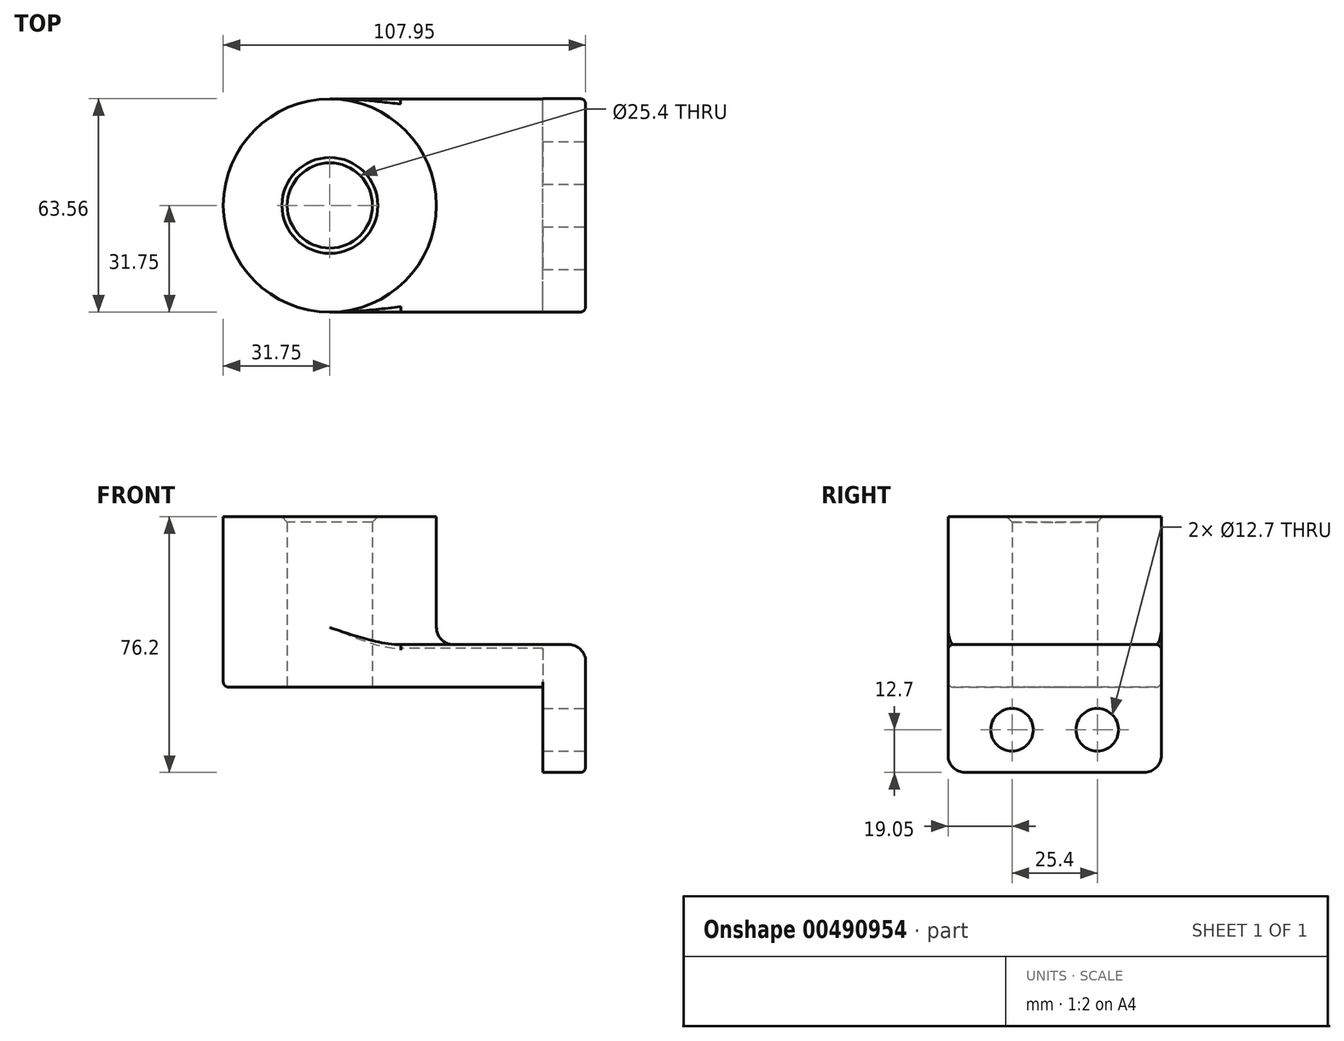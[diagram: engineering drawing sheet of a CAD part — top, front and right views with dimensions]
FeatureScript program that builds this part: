
annotation { "Feature Type Name" : "Feature", "Feature Type Description" : "" }
export const myFeature = defineFeature(function(context is Context, id is Id, definition is map)
    precondition{}
    {
        {
            var Q0;
            Q0=qCreatedBy(makeId("Top.planeOp"),FACE);
            var sketch = newSketch(context, id + "F0", { "sketchPlane" : qUnion([Q0])});
            skLineSegment(sketch, "E0.bottom", {"start": v(-38.1, 31.75) * mm, "end": v(38.1, 31.75) * mm});
            skLineSegment(sketch, "E0.top", {"start": v(-38.1, -31.75) * mm, "end": v(38.1, -31.75) * mm});
            skLineSegment(sketch, "E0.left", {"start": v(-38.1, 31.75) * mm, "end": v(-38.1, -31.75) * mm});
            skLineSegment(sketch, "E0.right", {"start": v(38.1, 31.75) * mm, "end": v(38.1, -31.75) * mm});
            skPoint(sketch, "E0.middle", {"position": v(0, 0) * mm});
            skCircle(sketch, "E1", {"center": v(-38.1, 0) * mm, "radius": 31.75 * mm});
            skCircle(sketch, "E2", {"center": v(-38.1, 0) * mm, "radius": 12.7 * mm});
            skSolve(sketch);
        }
        {
            var Q0;
            {var subQ0=sQuery(id+"F0.wireOp",EDGE,"E0.bottom");Q0=makeQuery(id+"F0.imprint","IMPRINT",FACE,{"disambiguationData":[TD([[makeQuery(id+"F0.imprint","IMPRINT",EDGE,{"derivedFrom":subQ0}),-1.0]])]});}
            var Q1;
            {var subQ1=sQuery(id+"F0.wireOp",EDGE,"E0.left");var subQ3=sQuery(id+"F0.wireOp",EDGE,"E2");var subQ4=makeQuery(id+"F0.imprint","INTERSECT",VERTEX,{"disambiguationData":[OD(0.0)],"derivedFrom":[subQ1,subQ3]});Q1=makeQuery(id+"F0.imprint","IMPRINT",FACE,{"disambiguationData":[TD([[makeQuery(id+"F0.imprint","IMPRINT",EDGE,{"disambiguationData":[TD([[subQ4,1.0]])],"derivedFrom":subQ3}),-1.0]])]});}
            var Q2;
            {var subQ1=sQuery(id+"F0.wireOp",EDGE,"E0.left");var subQ3=sQuery(id+"F0.wireOp",EDGE,"E2");var subQ4=makeQuery(id+"F0.imprint","INTERSECT",VERTEX,{"disambiguationData":[OD(0.0)],"derivedFrom":[subQ1,subQ3]});Q2=makeQuery(id+"F0.imprint","IMPRINT",FACE,{"disambiguationData":[TD([[makeQuery(id+"F0.imprint","IMPRINT",EDGE,{"disambiguationData":[TD([[subQ4,-1.0]])],"derivedFrom":subQ3}),-1.0]])]});}
            extrude(context, id + "F1", {"entities" : qUnion([Q0, Q1, Q2]), "depth" : 12.7 * mm});
        }
        {
            var Q0;
            {var subQ1=sQuery(id+"F0.wireOp",EDGE,"E0.left");var subQ3=sQuery(id+"F0.wireOp",EDGE,"E2");var subQ4=makeQuery(id+"F0.imprint","INTERSECT",VERTEX,{"disambiguationData":[OD(0.0)],"derivedFrom":[subQ1,subQ3]});Q0=makeQuery(id+"F0.imprint","IMPRINT",FACE,{"disambiguationData":[TD([[makeQuery(id+"F0.imprint","IMPRINT",EDGE,{"disambiguationData":[TD([[subQ4,-1.0]])],"derivedFrom":subQ3}),-1.0]])]});}
            var Q1;
            {var subQ1=sQuery(id+"F0.wireOp",EDGE,"E0.left");var subQ3=sQuery(id+"F0.wireOp",EDGE,"E2");var subQ4=makeQuery(id+"F0.imprint","INTERSECT",VERTEX,{"disambiguationData":[OD(0.0)],"derivedFrom":[subQ1,subQ3]});Q1=makeQuery(id+"F0.imprint","IMPRINT",FACE,{"disambiguationData":[TD([[makeQuery(id+"F0.imprint","IMPRINT",EDGE,{"disambiguationData":[TD([[subQ4,1.0]])],"derivedFrom":subQ3}),-1.0]])]});}
            extrude(context, id + "F2", {"entities" : qUnion([Q0, Q1]), "operationType" : NewBodyOperationType.ADD, "depth" : 50.8 * mm});
        }
        {
            var Q0;
            Q0=makeQuery(id+"F1.opExtrude","SWEPT_FACE",FACE,{"disambiguationData":[OSD([sQuery(id+"F0.wireOp",EDGE,"E0.right")])]});
            var sketch = newSketch(context, id + "F3", { "sketchPlane" : qUnion([Q0])});
            skLineSegment(sketch, "E3.bottom", {"start": v(-31.75, 12.7) * mm, "end": v(31.81, 12.7) * mm});
            skLineSegment(sketch, "E3.top", {"start": v(-31.75, -25.4) * mm, "end": v(31.81, -25.4) * mm});
            skLineSegment(sketch, "E3.left", {"start": v(-31.75, 12.7) * mm, "end": v(-31.75, -25.4) * mm});
            skLineSegment(sketch, "E3.right", {"start": v(31.81, 12.7) * mm, "end": v(31.81, -25.4) * mm});
            skCircle(sketch, "E4", {"center": v(-12.7, -12.7) * mm, "radius": 6.35 * mm});
            skLineSegment(sketch, "E5", {"start": v(0, 12.7) * mm, "end": v(0, -25.4) * mm});
            skCircle(sketch, "E6.MirrorC", {"center": v(12.7, -12.7) * mm, "radius": 6.35 * mm});
            skSolve(sketch);
        }
        {
            var Q0;
            {var subQ0=sQuery(id+"F3.wireOp",EDGE,"E3.left");var subQ1=sQuery(id+"F3.wireOp",EDGE,"E3.bottom");var subQ2=makeQuery(id+"F3.imprint","INTERSECT",VERTEX,{"derivedFrom":[subQ1,subQ0]});Q0=makeQuery(id+"F3.imprint","IMPRINT",FACE,{"disambiguationData":[TD([[makeQuery(id+"F3.imprint","IMPRINT",EDGE,{"disambiguationData":[TD([[subQ2,1.0]])],"derivedFrom":subQ1}),1.0]])]});}
            var Q1;
            {var subQ1=sQuery(id+"F0.wireOp",EDGE,"E0.right");var subQ2=makeQuery(id+"F1.opExtrude","SWEPT_EDGE",EDGE,{"disambiguationData":[OSD([sQuery(id+"F0.wireOp",EDGE,"E0.bottom"),subQ1])]});Q1=makeQuery(id+"F3.imprint","IMPRINT",FACE,{"disambiguationData":[TD([[makeQuery(id+"F3.imprint","IMPRINT",EDGE,{"derivedFrom":subQ2}),-1.0]])]});}
            var Q2;
            {var subQ6=sQuery(id+"F3.wireOp",EDGE,"E3.right");Q2=makeQuery(id+"F3.imprint","IMPRINT",FACE,{"disambiguationData":[TD([[makeQuery(id+"F3.imprint","IMPRINT",EDGE,{"derivedFrom":subQ6}),-1.0]])]});}
            var Q3;
            Q3=makeQuery(id+"F3.imprint","IMPRINT",FACE,{"disambiguationData":[TD([[makeQuery(id+"F3.imprint","IMPRINT",EDGE,{"derivedFrom":sQuery(id+"F3.wireOp",EDGE,"E4")}),-1.0]])]});
            extrude(context, id + "F4", {"entities" : qUnion([Q0, Q1, Q2, Q3]), "operationType" : NewBodyOperationType.ADD, "oppositeDirection" : true, "depth" : 12.7 * mm});
        }
        {
            var Q0;
            {var subQ0=sQuery(id+"F0.wireOp",EDGE,"E1");Q0=makeQuery(id+"F2.boolean.opBoolean","INTERSECT",EDGE,{"derivedFrom":[makeQuery(id+"F1.opExtrude","CAP_FACE",FACE,{"disambiguationData":[OSD([sQuery(id+"F0.wireOp",EDGE,"E0.bottom"),sQuery(id+"F0.wireOp",EDGE,"E0.top"),sQuery(id+"F0.wireOp",EDGE,"E0.right"),subQ0,sQuery(id+"F0.wireOp",EDGE,"E2")])],"isStart":false}),makeQuery(id+"F2.opExtrude","SWEPT_FACE",FACE,{"disambiguationData":[OSD([subQ0])]})]});}
            var Q1;
            Q1=makeQuery(id+"F4.opExtrude","SWEPT_EDGE",EDGE,{"disambiguationData":[OSD([sQuery(id+"F3.wireOp",EDGE,"E3.top"),sQuery(id+"F3.wireOp",EDGE,"E3.left")])]});
            var Q2;
            Q2=makeQuery(id+"F4.opExtrude","SWEPT_EDGE",EDGE,{"disambiguationData":[OSD([sQuery(id+"F3.wireOp",EDGE,"E3.top"),sQuery(id+"F3.wireOp",EDGE,"E3.right")])]});
            var Q3;
            Q3=makeQuery(id+"F4.boolean.opBoolean","MERGE",EDGE,{"derivedFrom":[makeQuery(id+"F1.opExtrude","CAP_EDGE",EDGE,{"disambiguationData":[OSD([sQuery(id+"F0.wireOp",EDGE,"E0.right")])],"isStart":false}),makeQuery(id+"F4.opExtrude","CAP_EDGE",EDGE,{"disambiguationData":[OSD([sQuery(id+"F3.wireOp",EDGE,"E3.bottom")])],"isStart":true})]});
            fillet(context, id + "F5", {"entities" : qUnion([Q0, Q1, Q2, Q3]), "radius" : 5.08 * mm, "tangentPropagation" : true, "allowEdgeOverflow" : false});
        }
        {
            var Q0;
            Q0=makeQuery(id+"F1.opExtrude","CAP_EDGE",EDGE,{"disambiguationData":[OSD([sQuery(id+"F0.wireOp",EDGE,"E0.top")])],"isStart":false});
            var Q1;
            Q1=makeQuery(id+"F1.opExtrude","CAP_EDGE",EDGE,{"disambiguationData":[OSD([sQuery(id+"F0.wireOp",EDGE,"E0.top")])],"isStart":true});
            fillet(context, id + "F6", {"entities" : qUnion([Q0, Q1]), "radius" : 1.59 * mm, "tangentPropagation" : true, "allowEdgeOverflow" : false});
        }
        {
            var Q0;
            Q0=makeQuery(id+"F2.opExtrude","CAP_EDGE",EDGE,{"disambiguationData":[OSD([sQuery(id+"F0.wireOp",EDGE,"E2")])],"isStart":false});
            chamfer(context, id + "F7", {"entities" : qUnion([Q0]), "width" : 1.59 * mm, "tangentPropagation" : true});
        }
    });
